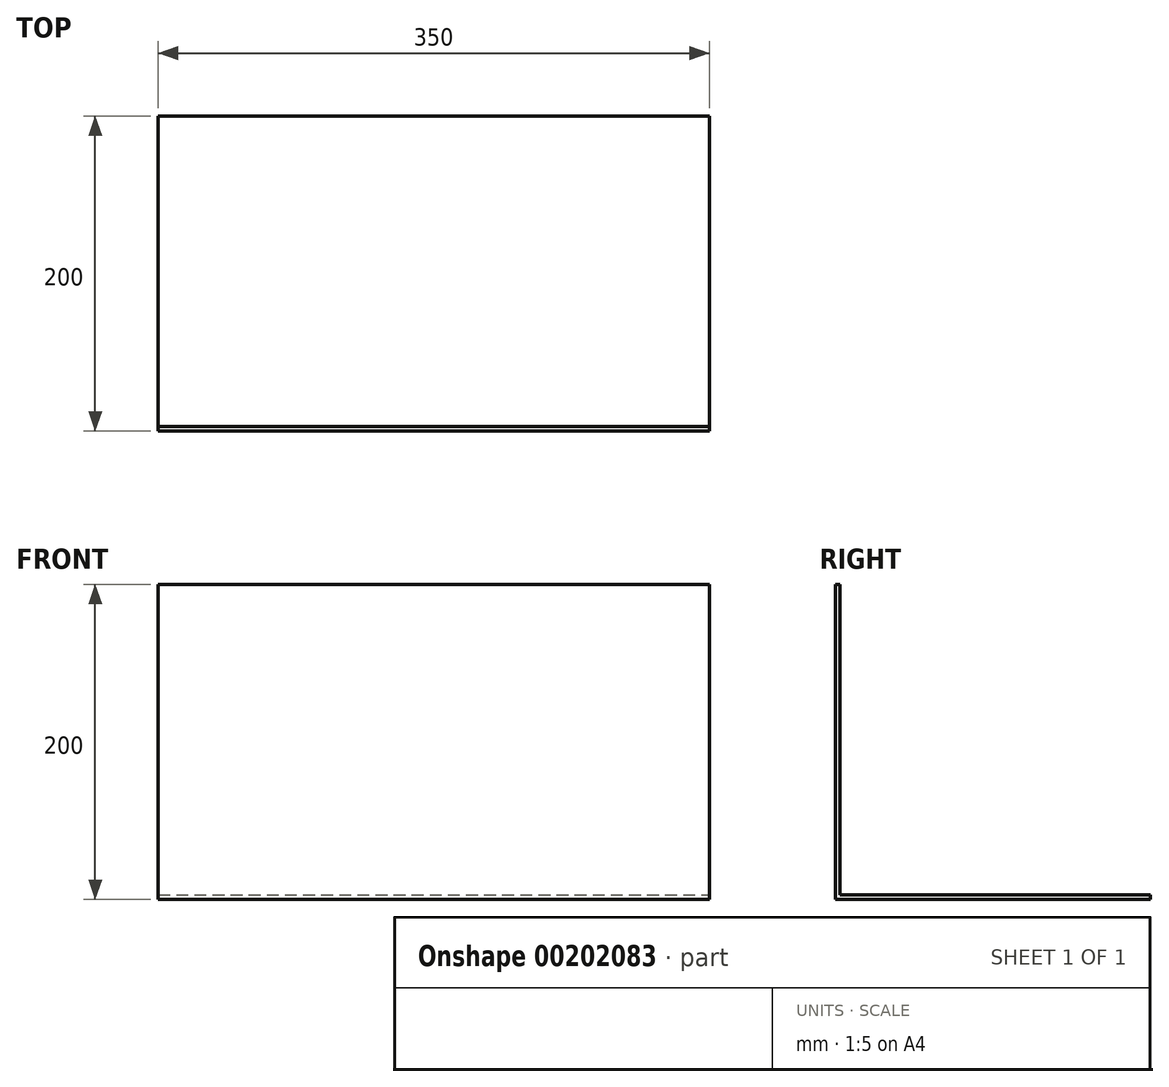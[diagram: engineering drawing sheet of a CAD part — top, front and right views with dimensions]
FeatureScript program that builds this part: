
annotation { "Feature Type Name" : "Feature", "Feature Type Description" : "" }
export const myFeature = defineFeature(function(context is Context, id is Id, definition is map)
    precondition{}
    {
        {
            var Q0;
            Q0=qCreatedBy(makeId("Top.planeOp"),FACE);
            var sketch = newSketch(context, id + "F0", { "sketchPlane" : qUnion([Q0])});
            skLineSegment(sketch, "E0.bottom", {"start": v(175, -100) * mm, "end": v(-175, -100) * mm});
            skLineSegment(sketch, "E0.top", {"start": v(175, 100) * mm, "end": v(-175, 100) * mm});
            skLineSegment(sketch, "E0.left", {"start": v(175, -100) * mm, "end": v(175, 100) * mm});
            skLineSegment(sketch, "E0.right", {"start": v(-175, -100) * mm, "end": v(-175, 100) * mm});
            skPoint(sketch, "E0.middle", {"position": v(0, 0) * mm});
            skSolve(sketch);
        }
        {
            var Q0;
            Q0=makeQuery(id+"F0.imprint","IMPRINT",FACE,{"disambiguationData":[TD([[makeQuery(id+"F0.imprint","IMPRINT",EDGE,{"derivedFrom":sQuery(id+"F0.wireOp",EDGE,"E0.bottom")}),-1.0]])]});
            extrude(context, id + "F1", {"entities" : qUnion([Q0]), "depth" : 3 * mm});
        }
        {
            var Q0;
            Q0=makeQuery(id+"F1.opExtrude","CAP_FACE",FACE,{"disambiguationData":[OSD([sQuery(id+"F0.wireOp",EDGE,"E0.bottom"),sQuery(id+"F0.wireOp",EDGE,"E0.top"),sQuery(id+"F0.wireOp",EDGE,"E0.left"),sQuery(id+"F0.wireOp",EDGE,"E0.right")])],"isStart":false});
            var sketch = newSketch(context, id + "F2", { "sketchPlane" : qUnion([Q0])});
            skLineSegment(sketch, "E1.bottom", {"start": v(-175, -100) * mm, "end": v(175, -100) * mm});
            skLineSegment(sketch, "E1.top", {"start": v(-175, -97) * mm, "end": v(175, -97) * mm});
            skLineSegment(sketch, "E1.left", {"start": v(-175, -100) * mm, "end": v(-175, -97) * mm});
            skLineSegment(sketch, "E1.right", {"start": v(175, -100) * mm, "end": v(175, -97) * mm});
            skSolve(sketch);
        }
        {
            var Q0;
            Q0 = qSketchRegion(id + "F2", true);
            extrude(context, id + "F3", {"entities" : qUnion([Q0]), "operationType" : NewBodyOperationType.ADD, "depth" : 197 * mm});
        }
    });
